# Revit family: BuroSeating_Konfurb_Duo_Block
name_source: partatom
category: Furniture
units: mm (PartAtom-declared; Revit-internal decimal feet)

## family parameters
Always vertical = Yes
Cut with Voids When Loaded = No
OmniClass Number = 23.40.70.14.64.11
OmniClass Title = Office Furniture
Room Calculation Point = No
Shared = No
Work Plane-Based = No

## types (10) — shared parameters
Assembly Code = E2020
BaseOffset = 4 mm  [stored 0.0131234 ft]
FeetMaterial = BuroSeating_Plastic_Grey
Manufacturer = Buro Seating
NominalDepth = 1230 mm  [stored 4.03543 ft]
NominalHeight = 400 mm  [stored 1.31234 ft]
NominalWidth = 1380 mm  [stored 4.52756 ft]
ProductGroup = Konfurb Duoblock
ProductPageURL AU = https://buroseating.com
ProductPageURL NZ = https://buroseating.co.nz
ProductRange = Konfurb
URL = https://buroseating.co.nz
URL AU = https://buroseating.com
WarrantyDescription = Full 5 year guarantee (excluding upholstery)
zero-valued in all types: Default Elevation

## per-type parameters (varying)
| type | BackFrameMaterial | Model | SeatMaterial |
| Konfurb Duoblock - White | BuroSeating_Polypropylene_White | KON516-0 | BuroSeating_Polypropylene_White |
| Konfurb Duoblock - Grey | BuroSeating_Polypropylene_Light Grey | KON516-2 | BuroSeating_Polypropylene_Light Grey |
| Konfurb Duoblock - Black | BuroSeating_Polypropylene_Black | KON516-3 | BuroSeating_Polypropylene_Black |
| Konfurb Duoblock - Blue | BuroSeating_Polypropylene_Blue | KON516-8 | BuroSeating_Polypropylene_Blue |
| Konfurb Duoblock - Yellow | BuroSeating_Polypropylene_Yellow | KON516-9 | BuroSeating_Polypropylene_Yellow |
| Konfurb Duoblock - Blue White | BuroSeating_Polypropylene_Blue | KON516-8-0 | BuroSeating_Polypropylene_White |
| Konfurb Duoblock - Blue Yellow | BuroSeating_Polypropylene_Yellow | KON516-8-9 | BuroSeating_Polypropylene_Blue |
| Konfurb Duoblock - White Yellow | BuroSeating_Polypropylene_Yellow | KON516-0-9 | BuroSeating_Polypropylene_White |
| Konfurb Duoblock - Blue Black | BuroSeating_Polypropylene_Black | KON516-8-3 | BuroSeating_Polypropylene_Blue |
| Konfurb Duoblock - White Black | BuroSeating_Polypropylene_Black | KON516-0-3 | BuroSeating_Polypropylene_White |

note: column(s) folded — value = type name in every type: Description

note: [stored X ft] marks values corroborated as IEEE doubles in the binary element streams (Revit-internal decimal feet)

## geometry (parser evidence)
native form markers: Sweep x6
no freeform markers — native parametric forms only
